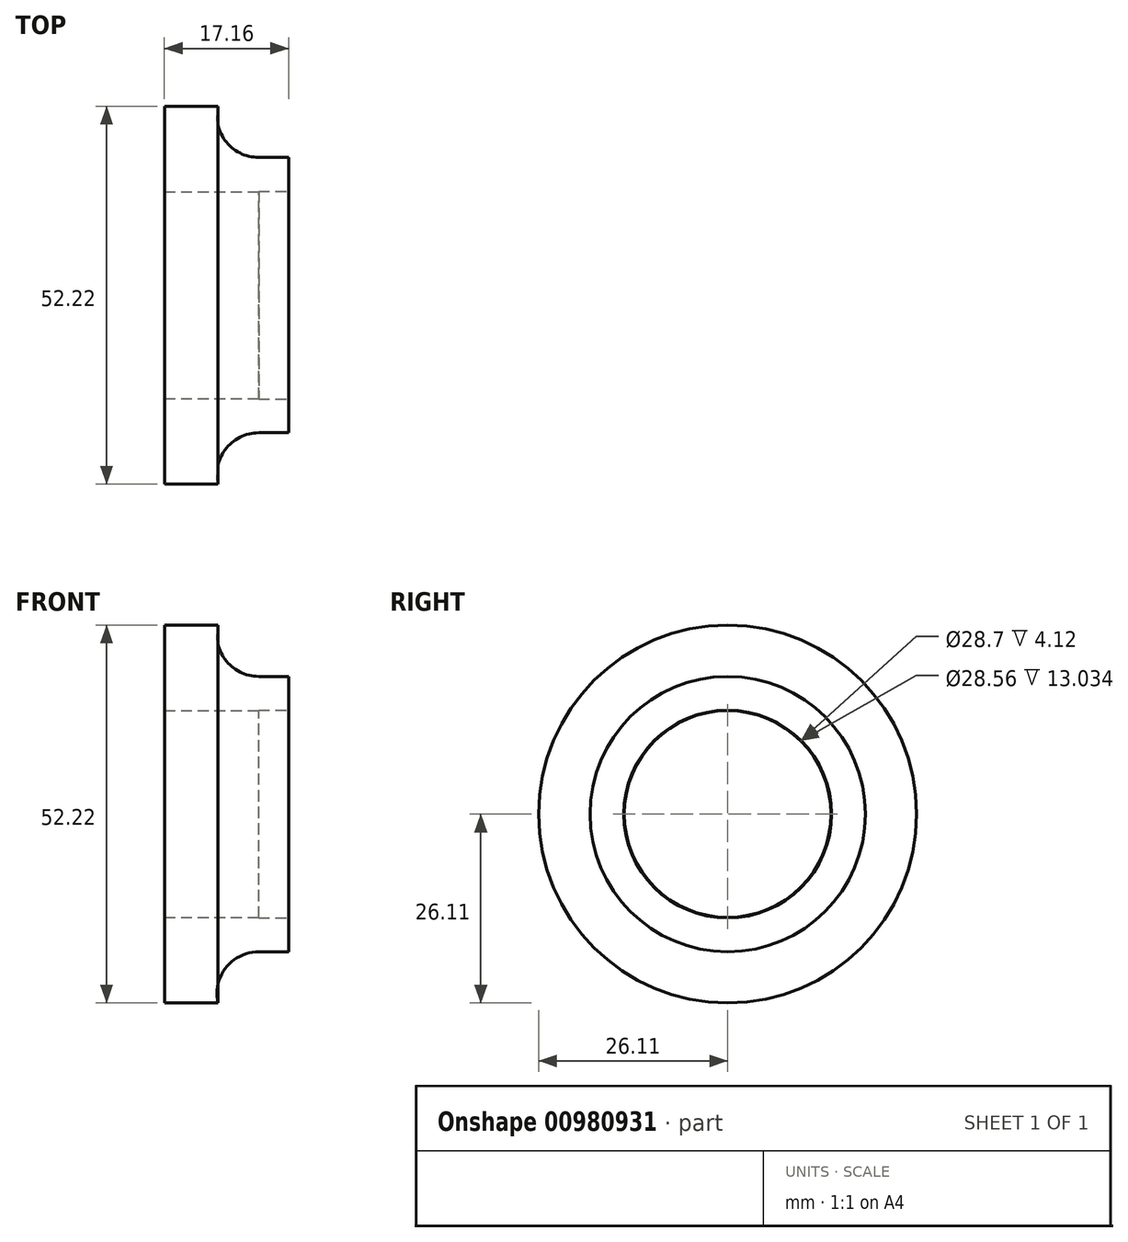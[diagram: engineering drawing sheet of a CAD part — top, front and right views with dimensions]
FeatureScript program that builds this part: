
annotation { "Feature Type Name" : "Feature", "Feature Type Description" : "" }
export const myFeature = defineFeature(function(context is Context, id is Id, definition is map)
    precondition{}
    {
        {
            var Q0;
            Q0=qCreatedBy(makeId("Front.planeOp"),FACE);
            var sketch = newSketch(context, id + "F0", { "sketchPlane" : qUnion([Q0])});
            skLineSegment(sketch, "E0", {"start": v(-34.6, 14.35) * mm, "end": v(-34.6, 14.28) * mm});
            skLineSegment(sketch, "E1", {"start": v(-34.6, 14.28) * mm, "end": v(-47.63, 14.28) * mm});
            skLineSegment(sketch, "E2", {"start": v(-47.63, 14.28) * mm, "end": v(-47.63, 26.11) * mm});
            skLineSegment(sketch, "E3", {"start": v(-47.63, 26.11) * mm, "end": v(-40.24, 26.11) * mm});
            skArc(sketch, "E4", {"start": v(-40.24, 26.11) * mm, "mid": v(-39.12, 21.21) * mm, "end": v(-34.6, 19.03) * mm});
            skLineSegment(sketch, "E5", {"start": v(0, 0) * mm, "end": v(-63.07, 0) * mm, "construction": true});
            skLineSegment(sketch, "E6.bottom", {"start": v(-34.6, 19.03) * mm, "end": v(-30.47, 19.03) * mm});
            skLineSegment(sketch, "E6.top", {"start": v(-34.6, 14.35) * mm, "end": v(-30.47, 14.35) * mm});
            skLineSegment(sketch, "E6.right", {"start": v(-30.47, 19.03) * mm, "end": v(-30.47, 14.35) * mm});
            skSolve(sketch);
        }
        {
            var Q0;
            Q0=makeQuery(id+"F0.imprint","IMPRINT",FACE,{"disambiguationData":[TD([[makeQuery(id+"F0.imprint","IMPRINT",EDGE,{"derivedFrom":sQuery(id+"F0.wireOp",EDGE,"E0")}),-1.0]])]});
            var Q1;
            Q1=sQuery(id+"F0.wireOp",EDGE,"E5");
            revolve(context, id + "F1", {"surfaceOperationType" : NewSurfaceOperationType.NEW, "entities" : qUnion([Q0]), "axis" : qUnion([Q1]), "revolveType" : RevolveType.FULL});
        }
    });
